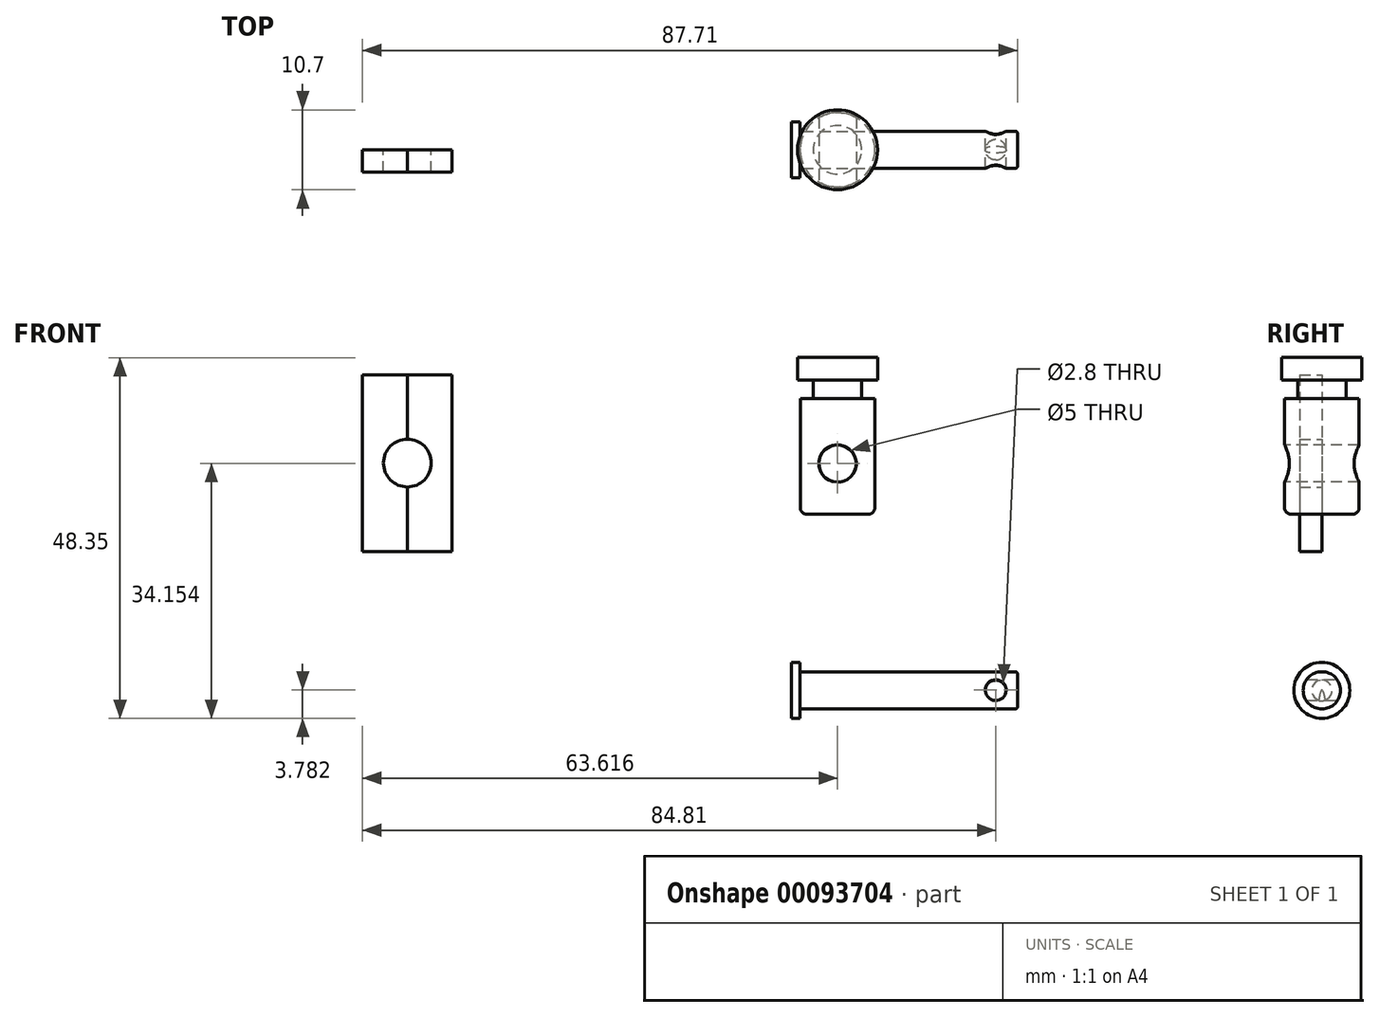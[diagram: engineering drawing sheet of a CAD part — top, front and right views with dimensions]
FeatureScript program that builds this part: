
annotation { "Feature Type Name" : "Feature", "Feature Type Description" : "" }
export const myFeature = defineFeature(function(context is Context, id is Id, definition is map)
    precondition{}
    {
        {
            var Q0;
            Q0=qCreatedBy(makeId("Front.planeOp"),FACE);
            var sketch = newSketch(context, id + "F0", { "sketchPlane" : qUnion([Q0])});
            skLineSegment(sketch, "E0", {"start": v(-11.17, 44.6) * mm, "end": v(-0.47, 44.6) * mm});
            skLineSegment(sketch, "E1", {"start": v(-0.47, 44.6) * mm, "end": v(-0.47, 41.6) * mm});
            skLineSegment(sketch, "E2", {"start": v(-0.47, 41.6) * mm, "end": v(-2.57, 41.6) * mm});
            skLineSegment(sketch, "E3", {"start": v(-2.57, 41.6) * mm, "end": v(-2.57, 39.1) * mm});
            skLineSegment(sketch, "E4", {"start": v(-2.57, 39.1) * mm, "end": v(-0.82, 39.1) * mm});
            skLineSegment(sketch, "E5", {"start": v(-0.82, 39.1) * mm, "end": v(-0.82, 24.5) * mm});
            skLineSegment(sketch, "E6", {"start": v(-1.72, 23.6) * mm, "end": v(-9.93, 23.6) * mm});
            skLineSegment(sketch, "E7", {"start": v(-10.82, 24.5) * mm, "end": v(-10.82, 39.1) * mm});
            skLineSegment(sketch, "E8", {"start": v(-10.82, 39.1) * mm, "end": v(-9.07, 39.1) * mm});
            skLineSegment(sketch, "E9", {"start": v(-9.07, 39.1) * mm, "end": v(-9.07, 41.6) * mm});
            skLineSegment(sketch, "E10", {"start": v(-9.07, 41.6) * mm, "end": v(-11.17, 41.6) * mm});
            skLineSegment(sketch, "E11", {"start": v(-11.17, 41.6) * mm, "end": v(-11.17, 44.6) * mm});
            skLineSegment(sketch, "E12", {"start": v(-5.82, 44.6) * mm, "end": v(-5.82, 39.1) * mm, "construction": true});
            skLineSegment(sketch, "E13", {"start": v(-9.07, 41.6) * mm, "end": v(-5.82, 41.6) * mm, "construction": true});
            skLineSegment(sketch, "E14", {"start": v(-5.82, 41.6) * mm, "end": v(-2.57, 41.6) * mm, "construction": true});
            skLineSegment(sketch, "E15", {"start": v(-5.82, 39.1) * mm, "end": v(-5.82, 23.6) * mm, "construction": true});
            skCircle(sketch, "E16", {"center": v(-5.82, 30.4) * mm, "radius": 2.5 * mm});
            skLineSegment(sketch, "E17", {"start": v(-5.82, 44.6) * mm, "end": v(-5.82, 32.9) * mm});
            skLineSegment(sketch, "E18.trimOffspring", {"start": v(-5.82, 27.9) * mm, "end": v(-5.82, 23.6) * mm});
            skPoint(sketch, "E19.visualSharp", {"position": v(-10.82, 23.6) * mm});
            skArc(sketch, "E19.filletArc", {"start": v(-10.82, 24.5) * mm, "mid": v(-10.56, 23.87) * mm, "end": v(-9.93, 23.6) * mm});
            skPoint(sketch, "E20.visualSharp", {"position": v(-0.82, 23.6) * mm});
            skArc(sketch, "E20.filletArc", {"start": v(-1.72, 23.6) * mm, "mid": v(-1.09, 23.87) * mm, "end": v(-0.82, 24.5) * mm});
            skLineSegment(sketch, "E21", {"start": v(-10.82, 30.4) * mm, "end": v(-8.32, 30.4) * mm, "construction": true});
            skSolve(sketch);
        }
        {
            var Q0;
            {var subQ0=sQuery(id+"F0.wireOp",EDGE,"E1");Q0=makeQuery(id+"F0.imprint","IMPRINT",FACE,{"disambiguationData":[TD([[makeQuery(id+"F0.imprint","IMPRINT",EDGE,{"derivedFrom":subQ0}),-1.0]])]});}
            var Q1;
            Q1=sQuery(id+"F0.wireOp",EDGE,"E15");
            revolve(context, id + "F1", {"entities" : qUnion([Q0]), "axis" : qUnion([Q1]), "revolveType" : RevolveType.FULL});
        }
        {
            var Q0;
            {var subQ0=sQuery(id+"F0.wireOp",EDGE,"E16");var subQ1=makeQuery(id+"F0.imprint","INTERSECT",VERTEX,{"derivedFrom":[subQ0,sQuery(id+"F0.wireOp",EDGE,"E17")]});Q0=makeQuery(id+"F0.imprint","IMPRINT",FACE,{"disambiguationData":[TD([[makeQuery(id+"F0.imprint","IMPRINT",EDGE,{"disambiguationData":[TD([[subQ1,-1.0]])],"derivedFrom":subQ0}),1.0]])]});}
            extrude(context, id + "F2", {"entities" : qUnion([Q0]), "operationType" : NewBodyOperationType.REMOVE, "oppositeDirection" : true, "depth" : 25 * mm, "symmetric" : true});
        }
        {
            var Q0;
            Q0=qCreatedBy(makeId("Front.planeOp"),FACE);
            var sketch = newSketch(context, id + "F3", { "sketchPlane" : qUnion([Q0])});
            skLineSegment(sketch, "E22", {"start": v(-12.03, 3.75) * mm, "end": v(-10.83, 3.75) * mm});
            skLineSegment(sketch, "E23", {"start": v(-10.83, 3.75) * mm, "end": v(-10.83, 2.5) * mm});
            skLineSegment(sketch, "E24", {"start": v(-10.83, 2.5) * mm, "end": v(17.97, 2.5) * mm});
            skLineSegment(sketch, "E25", {"start": v(18.27, 2.2) * mm, "end": v(18.27, 0.3) * mm});
            skLineSegment(sketch, "E26", {"start": v(-12.03, 0) * mm, "end": v(-12.03, 3.75) * mm});
            skLineSegment(sketch, "E27", {"start": v(15.37, 2.5) * mm, "end": v(15.37, -1.37) * mm, "construction": true});
            skCircle(sketch, "E28", {"center": v(15.37, 0.03) * mm, "radius": 1.4 * mm});
            skLineSegment(sketch, "E29", {"start": v(18.27, 0) * mm, "end": v(-12.03, 0) * mm, "construction": true});
            skLineSegment(sketch, "E30", {"start": v(17.97, 0) * mm, "end": v(16.77, 0) * mm});
            skLineSegment(sketch, "E31", {"start": v(-12.03, 0) * mm, "end": v(13.97, 0) * mm});
            skPoint(sketch, "E32.visualSharp", {"position": v(18.27, 2.5) * mm});
            skArc(sketch, "E32.filletArc", {"start": v(18.27, 2.2) * mm, "mid": v(18.18, 2.41) * mm, "end": v(17.97, 2.5) * mm});
            skPoint(sketch, "E33.visualSharp", {"position": v(18.27, 0) * mm});
            skArc(sketch, "E33.filletArc", {"start": v(17.97, 0) * mm, "mid": v(18.18, 0.09) * mm, "end": v(18.27, 0.3) * mm});
            skSolve(sketch);
        }
        {
            var Q0;
            Q0=makeQuery(id+"F3.imprint","IMPRINT",FACE,{"disambiguationData":[TD([[makeQuery(id+"F3.imprint","IMPRINT",EDGE,{"derivedFrom":sQuery(id+"F3.wireOp",EDGE,"E22")}),-1.0]])]});
            var Q1;
            Q1=sQuery(id+"F3.wireOp",EDGE,"E29");
            revolve(context, id + "F4", {"entities" : qUnion([Q0]), "axis" : qUnion([Q1]), "revolveType" : RevolveType.FULL});
        }
        {
            var Q0;
            {var subQ0=sQuery(id+"F3.wireOp",EDGE,"E28");var subQ1=makeQuery(id+"F3.imprint","INTERSECT",VERTEX,{"derivedFrom":[subQ0,sQuery(id+"F3.wireOp",EDGE,"E30")]});Q0=makeQuery(id+"F3.imprint","IMPRINT",FACE,{"disambiguationData":[TD([[makeQuery(id+"F3.imprint","IMPRINT",EDGE,{"disambiguationData":[TD([[subQ1,1.0]])],"derivedFrom":subQ0}),1.0]])]});}
            var Q1;
            Q1=sQuery(id+"F3.wireOp",EDGE,"E28");
            extrude(context, id + "F5", {"entities" : qUnion([Q0]), "operationType" : NewBodyOperationType.REMOVE, "surfaceEntities" : qUnion([Q1]), "depth" : 5 * mm, "symmetric" : true});
        }
        {
            var Q0;
            Q0=qCreatedBy(makeId("Front.planeOp"),FACE);
            var sketch = newSketch(context, id + "F6", { "sketchPlane" : qUnion([Q0])});
            skLineSegment(sketch, "E34.bottom", {"start": v(-69.44, 42.31) * mm, "end": v(-57.44, 42.31) * mm});
            skLineSegment(sketch, "E34.top", {"start": v(-69.44, 18.61) * mm, "end": v(-57.44, 18.61) * mm});
            skLineSegment(sketch, "E34.left", {"start": v(-69.44, 42.31) * mm, "end": v(-69.44, 18.61) * mm});
            skLineSegment(sketch, "E34.right", {"start": v(-57.44, 42.31) * mm, "end": v(-57.44, 18.61) * mm});
            skLineSegment(sketch, "E35", {"start": v(-63.44, 42.31) * mm, "end": v(-63.44, 18.61) * mm, "construction": true});
            skLineSegment(sketch, "E36", {"start": v(-69.44, 30.46) * mm, "end": v(-57.44, 30.46) * mm, "construction": true});
            skCircle(sketch, "E37", {"center": v(-63.44, 30.46) * mm, "radius": 3.2 * mm});
            skLineSegment(sketch, "E38", {"start": v(-63.44, 42.31) * mm, "end": v(-63.44, 33.66) * mm});
            skLineSegment(sketch, "E39", {"start": v(-63.44, 27.26) * mm, "end": v(-63.44, 18.61) * mm});
            skSolve(sketch);
        }
        {
            var Q0;
            {var subQ3=sQuery(id+"F6.wireOp",EDGE,"E34.right");Q0=makeQuery(id+"F6.imprint","IMPRINT",FACE,{"disambiguationData":[TD([[makeQuery(id+"F6.imprint","IMPRINT",EDGE,{"derivedFrom":subQ3}),-1.0]])]});}
            extrude(context, id + "F7", {"entities" : qUnion([Q0]), "depth" : 3 * mm});
        }
        {
            var Q0;
            {var subQ3=sQuery(id+"F6.wireOp",EDGE,"E34.left");Q0=makeQuery(id+"F6.imprint","IMPRINT",FACE,{"disambiguationData":[TD([[makeQuery(id+"F6.imprint","IMPRINT",EDGE,{"derivedFrom":subQ3}),1.0]])]});}
            extrude(context, id + "F8", {"entities" : qUnion([Q0]), "depth" : 3 * mm});
        }
    });
